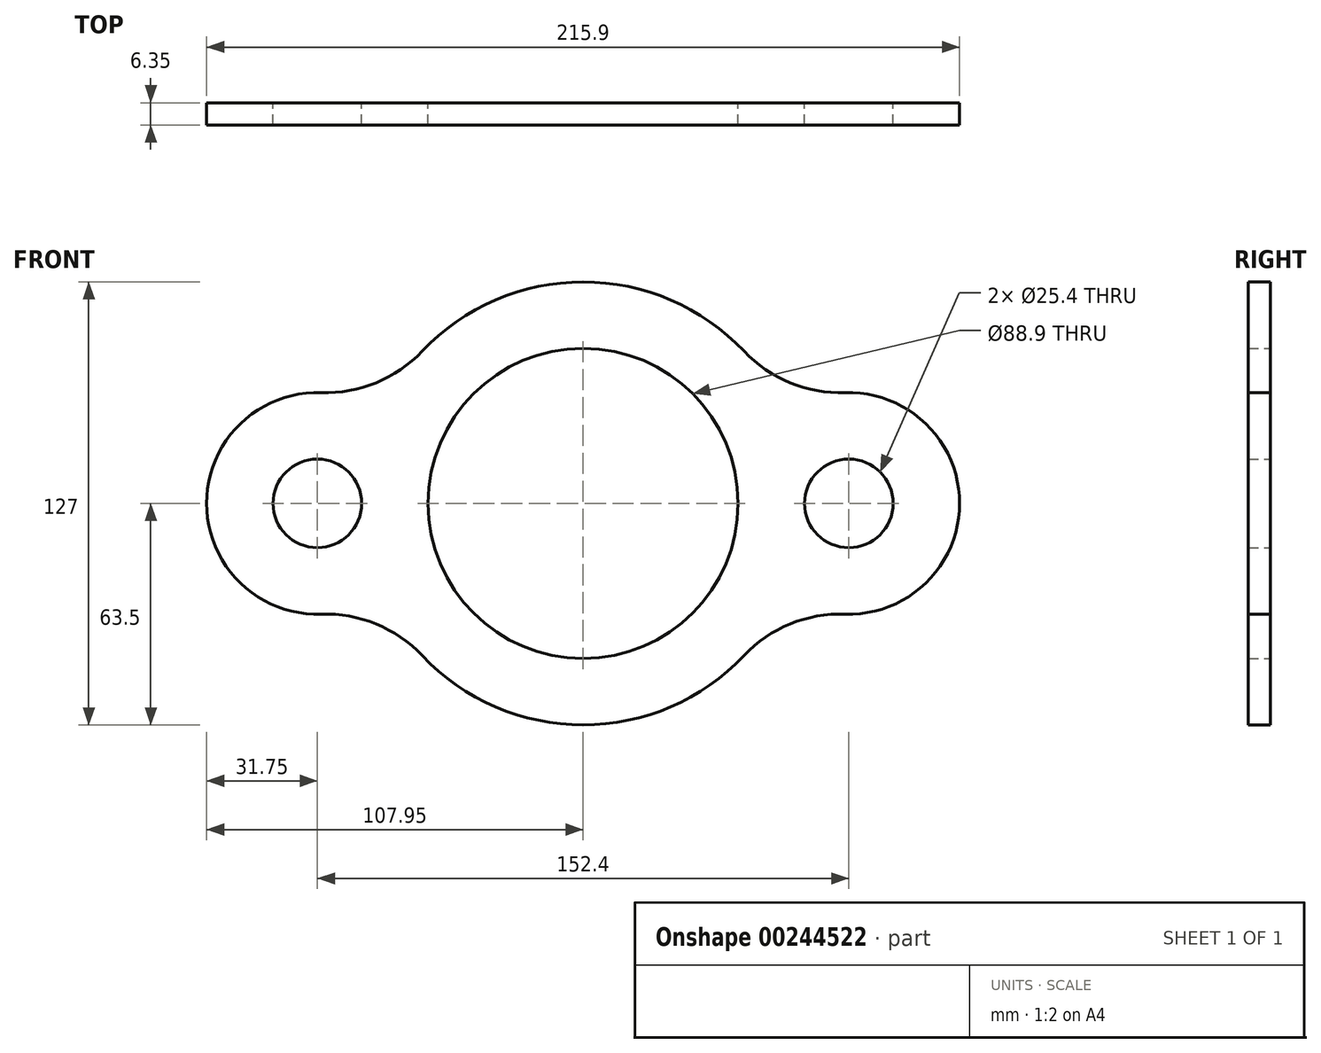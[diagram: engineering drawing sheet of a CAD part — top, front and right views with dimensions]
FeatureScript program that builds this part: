
annotation { "Feature Type Name" : "Feature", "Feature Type Description" : "" }
export const myFeature = defineFeature(function(context is Context, id is Id, definition is map)
    precondition{}
    {
        {
            var Q0;
            Q0=qCreatedBy(makeId("Front.planeOp"),FACE);
            var sketch = newSketch(context, id + "F0", { "sketchPlane" : qUnion([Q0])});
            skCircle(sketch, "E0", {"center": v(0, 0) * mm, "radius": 44.45 * mm});
            skArc(sketch, "E1", {"start": v(-46.14, -43.63) * mm, "mid": v(0, -63.5) * mm, "end": v(46.14, -43.63) * mm});
            skCircle(sketch, "E2", {"center": v(76.2, 0) * mm, "radius": 12.7 * mm});
            skCircle(sketch, "E3", {"center": v(-76.2, 0) * mm, "radius": 12.7 * mm});
            skArc(sketch, "E4", {"start": v(75.12, -31.73) * mm, "mid": v(107.95, 0) * mm, "end": v(75.12, 31.73) * mm});
            skArc(sketch, "E5", {"start": v(-75.12, 31.73) * mm, "mid": v(-107.95, 0) * mm, "end": v(-75.12, -31.73) * mm});
            skArc(sketch, "E6.trimOffspring", {"start": v(46.14, 43.63) * mm, "mid": v(0, 63.5) * mm, "end": v(-46.14, 43.63) * mm});
            skPoint(sketch, "E7.visualSharp", {"position": v(57.94, 25.98) * mm});
            skArc(sketch, "E7.filletArc", {"start": v(46.14, 43.63) * mm, "mid": v(59.35, 34.56) * mm, "end": v(75.12, 31.73) * mm});
            skPoint(sketch, "E8.visualSharp", {"position": v(57.94, -25.98) * mm});
            skArc(sketch, "E8.filletArc", {"start": v(75.12, -31.73) * mm, "mid": v(59.35, -34.56) * mm, "end": v(46.14, -43.63) * mm});
            skPoint(sketch, "E9.visualSharp", {"position": v(-57.94, -25.98) * mm});
            skArc(sketch, "E9.filletArc", {"start": v(-46.14, -43.63) * mm, "mid": v(-59.35, -34.56) * mm, "end": v(-75.12, -31.73) * mm});
            skPoint(sketch, "E10.visualSharp", {"position": v(-57.94, 25.98) * mm});
            skArc(sketch, "E10.filletArc", {"start": v(-75.12, 31.73) * mm, "mid": v(-59.35, 34.56) * mm, "end": v(-46.14, 43.63) * mm});
            skSolve(sketch);
        }
        {
            var Q0;
            Q0=makeQuery(id+"F0.imprint","IMPRINT",FACE,{"disambiguationData":[TD([[makeQuery(id+"F0.imprint","IMPRINT",EDGE,{"derivedFrom":sQuery(id+"F0.wireOp",EDGE,"E0")}),-1.0]])]});
            extrude(context, id + "F1", {"entities" : qUnion([Q0]), "depth" : 6.35 * mm});
        }
    });
